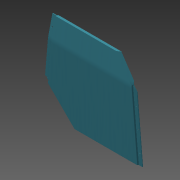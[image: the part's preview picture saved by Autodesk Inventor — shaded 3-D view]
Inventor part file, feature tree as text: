
AUTODESK INVENTOR PART (.ipt)
format: ipt  version: 2015 (Build 190159000, 159)  size: 1,082,368 bytes
history: native  units: mm
features: sketch x7, other x5, fillet x3, hole x2, extrude x2, loft x1, mirror x1, shell x1
ambient origin geometry x8: Origin, YZ Plane, XZ Plane, XY Plane, X Axis, Y Axis, Z Axis, Center Point
bodies: Body1 (feature_tree)
feature tree (22):
  sketch  "Szkic1"
  other  "Płaszczyzna konstrukcyjna2"
  loft  "Wyciągnięcie złożone2"
  other  "Płaszczyzna konstrukcyjna3"
  other  "Podział1"
  mirror  "Odbicie lustrzane1"
  shell  "Skorupa1"  Thickness=1.0mm
  fillet  "Zaokrąglenie1"  Radius=1.0mm
  fillet  "Zaokrąglenie3"  Radius=3.0mm
  hole  "Otwór3"  [1 undecoded]
  other  "Gięcie części2"
  extrude  "Wyciągnięcie proste6"  Depth=11.5mm
  extrude  "Wyciągnięcie proste7"  Depth=2.0mm
  fillet  "Zaokrąglenie5"  Radius=0.4mm
  hole  "Otwór4"  [1 undecoded]
  sketch  "Szkic9"
  other  "Bryła3"
  sketch  "Szkic11"
  sketch  "Szkic12"
  sketch  "Szkic14"
  sketch  "Szkic15"
  sketch  "Szkic16"
note: 2 required parameter values undecoded (feature->parameter linkage not recoverable at this tier; creation-order binding heuristic only, values carry confidence <= 0.55)
